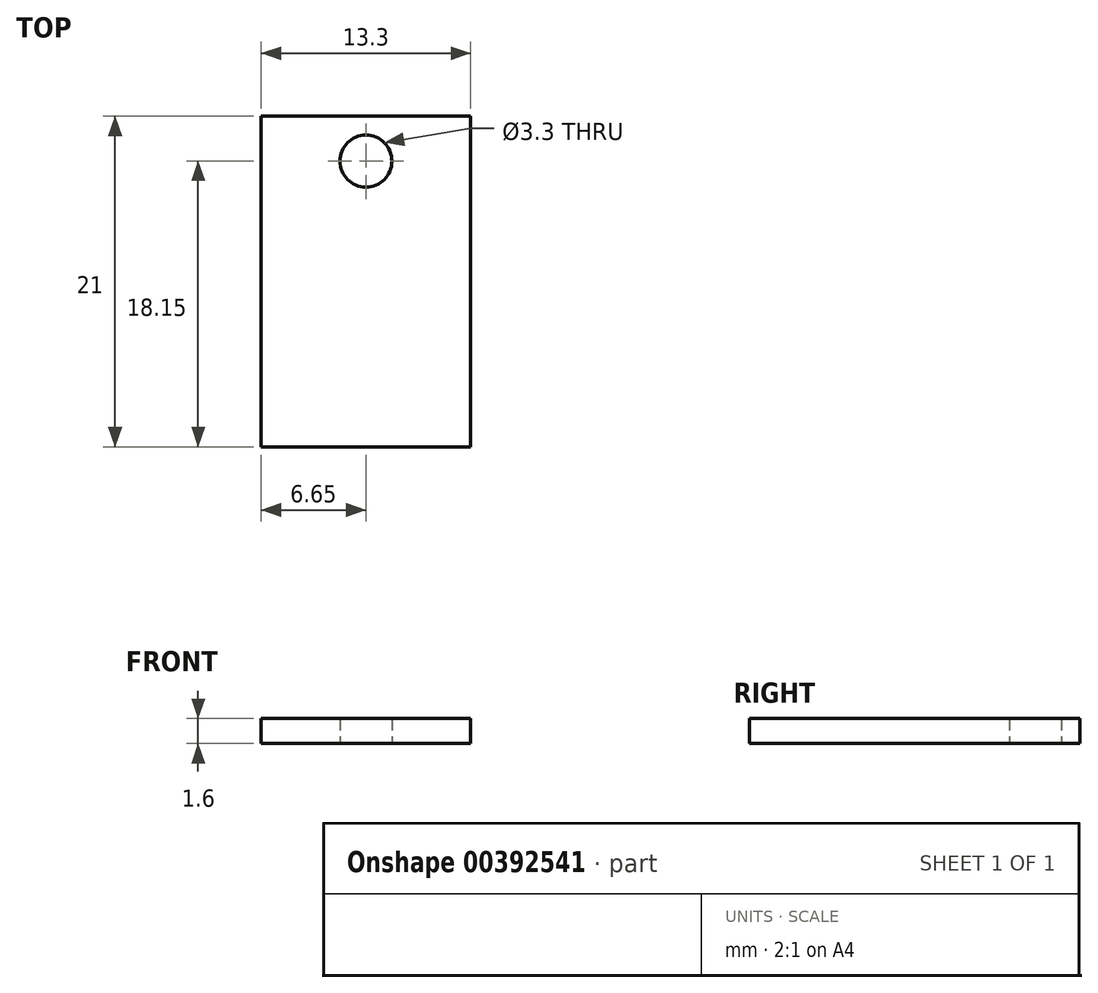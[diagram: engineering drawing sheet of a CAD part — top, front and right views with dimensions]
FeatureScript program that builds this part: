
annotation { "Feature Type Name" : "Feature", "Feature Type Description" : "" }
export const myFeature = defineFeature(function(context is Context, id is Id, definition is map)
    precondition{}
    {
        {
            var Q0;
            Q0=qCreatedBy(makeId("Top.planeOp"),FACE);
            var sketch = newSketch(context, id + "F0", { "sketchPlane" : qUnion([Q0])});
            skLineSegment(sketch, "E0.bottom", {"start": v(6.65, 21) * mm, "end": v(-6.65, 21) * mm});
            skLineSegment(sketch, "E0.top", {"start": v(6.65, 0) * mm, "end": v(-6.65, 0) * mm});
            skLineSegment(sketch, "E0.left", {"start": v(6.65, 21) * mm, "end": v(6.65, 0) * mm});
            skLineSegment(sketch, "E0.right", {"start": v(-6.65, 21) * mm, "end": v(-6.65, 0) * mm});
            skCircle(sketch, "E1", {"center": v(0, 18.15) * mm, "radius": 1.65 * mm});
            skPoint(sketch, "E1.centerSnap0", {"position": v(0, 21) * mm});
            skSolve(sketch);
        }
        {
            var Q0;
            Q0=makeQuery(id+"F0.imprint","IMPRINT",FACE,{"disambiguationData":[TD([[makeQuery(id+"F0.imprint","IMPRINT",EDGE,{"derivedFrom":sQuery(id+"F0.wireOp",EDGE,"E0.bottom")}),1.0]])]});
            extrude(context, id + "F1", {"entities" : qUnion([Q0]), "depth" : 1.6 * mm});
        }
    });
